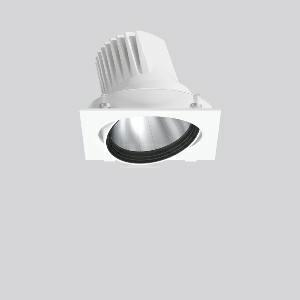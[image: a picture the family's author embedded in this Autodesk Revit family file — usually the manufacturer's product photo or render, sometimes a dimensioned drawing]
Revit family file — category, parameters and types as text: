
# Revit family: magcardo_maxi_722207_002_23f5
name_source: partatom
category: Lighting Fixtures
units: mm (PartAtom-declared; Revit-internal decimal feet)

## family parameters
Cut with Voids When Loaded = No
Host = Face
Light Source = No
Part Type = Normal
Room Calculation Point = No
Round Connector Dimension = Use Diameter
Shared = No

## types (1)
- MAGCARDO maxi (1 x LED Modul 920 meat+, 2200 lm, 2000)
    Apparent Load = 33 VA
    Approval mark = CE
    CIE Flux Codes = 100 100 100 100 100
    Color Rendering = 90
    Color Temperature = 2000
    Default Elevation = 1800 mm
    Description = Series: MAGCARDO maxi
Projector unit for tool-free mounting in separate recessed frame. Luminaire top: die-cast aluminium, powder-coated. Rotation range 356° and swivel range ± 35°. Inner cover prevents view into the false ceiling. Black plastic ring and recessed LED to prevent glare from the side. Optical assembly with reflector made of MIRO-Silver with 98% total light reflection for outstanding efficiency - can be changed without tools. Special LED for illumination of meat included. Magnetic click locking mechanism for quick and convenient installation without tools: insert the recessed frame (1, 2 or 3-lamp) with clamp fastener (no tools required), push the luminaire head with the base plate into the recessed frame and fix magnetically. Including separate LED converter with connecting cable 600 mm.High quality converter without flickering and stroboscopic effect. Through-wiring box (5 pole) available as accessory. The following accessories can be mounted without use of tools: interchangeable lenses, honeycomb louvre, clear and frosted diffusers, white interchangeable plastic ring.Modular design: recessed mounting frame must be ordered separately! 
Colour: traffic white, matt (RAL 9016)
Length: 172 mm
Width: 167 mm
Height: 137 mm
Recess height: 155 mm
Lamp: LED
Socket: without socket
Colour temperature: meat +
System power: 33 W
Rated luminous flux: 2200 lm
Luminous efficiency: 67 lm/W
Control gear: Regulated power supply
Protection class: II
Type of protection: IP 20
    Height = 0 mm  [stored 0 ft]
    Lamp = 1 x LED Modul 920 meat+
    Lamp Light Flux = 2200 lm
    Lamp count = 1
    Length = 172 mm
    Lifetime = 50000 h
    Luminous efficacy = 67 lm/W
    Manufacturer = RZB
    ModVariant = No
    Model = 722207.002
    Mounting Place = Ceiling, Wall
    Mounting Type = Recessed
    Number of Poles = 1
    OnlyDefault = Yes
    Power Factor = 1
    Product Name = MAGCARDO maxi
    Product group = Recessed projectors
    ProductGroupID = 401
    Protection Class = Protection class II
    Protection Degree = IP 20
    RLX_Detail_Level = 1
    RLX_Emergency_Light_Flux = 0 lm
    RLX_Emergency_Type = 0
    RLX_Emergency_Type_DB = No
    RlxData = <blob elided: 40009 chars, md5=a313baa6>
    Socket = socket
    Standby Power = 0 W
    System Light Flux = 2200 lm
    System Power = 33 W
    Type Comments = Product without accessories
    Type Image = 722045.002.jpg
    URL = http://relux.com
    VarID = ---
    Voltage = 230 V
    Voltage Range = 220-240 V
    Weight = 0.00 kg
    Width = 167 mm

note: [stored X ft] marks values corroborated as IEEE doubles in the binary element streams (Revit-internal decimal feet)

## geometry (parser evidence)
native form markers: Blend x4, Sweep x13
no freeform markers — native parametric forms only
